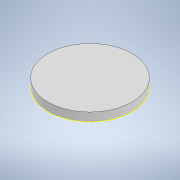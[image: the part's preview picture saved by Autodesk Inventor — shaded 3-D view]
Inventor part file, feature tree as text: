
AUTODESK INVENTOR PART (.ipt)
format: ipt  version: 2020 (Build 240168000, 168)  size: 282,624 bytes
history: native  units: in
note: dims shown in document units (in); Inventor stores cm internally (conversion verified against a paired STEP export)
features: other x3, fillet x2, sketch x2, boolean_combine x1
ambient origin geometry x8: Origin, YZ Plane, XZ Plane, XY Plane, X Axis, Y Axis, Z Axis, Center Point
bodies: Solid1 (feature_tree), Solid2 (feature_tree)
feature tree (8):
  other  "Alliance Marker - Blue.iam"
  other  "Alliance Marker - Blue.ipt:1"
  other  "Mount Male.ipt:1"
  boolean_combine  "Combine1"
  fillet  "Fillet1"  Radius=0.3937in
  fillet  "Fillet2"  Radius=0.4in
  sketch  "Sketch3"  dims[d2=0.1in]
  sketch  "Sketch5"
